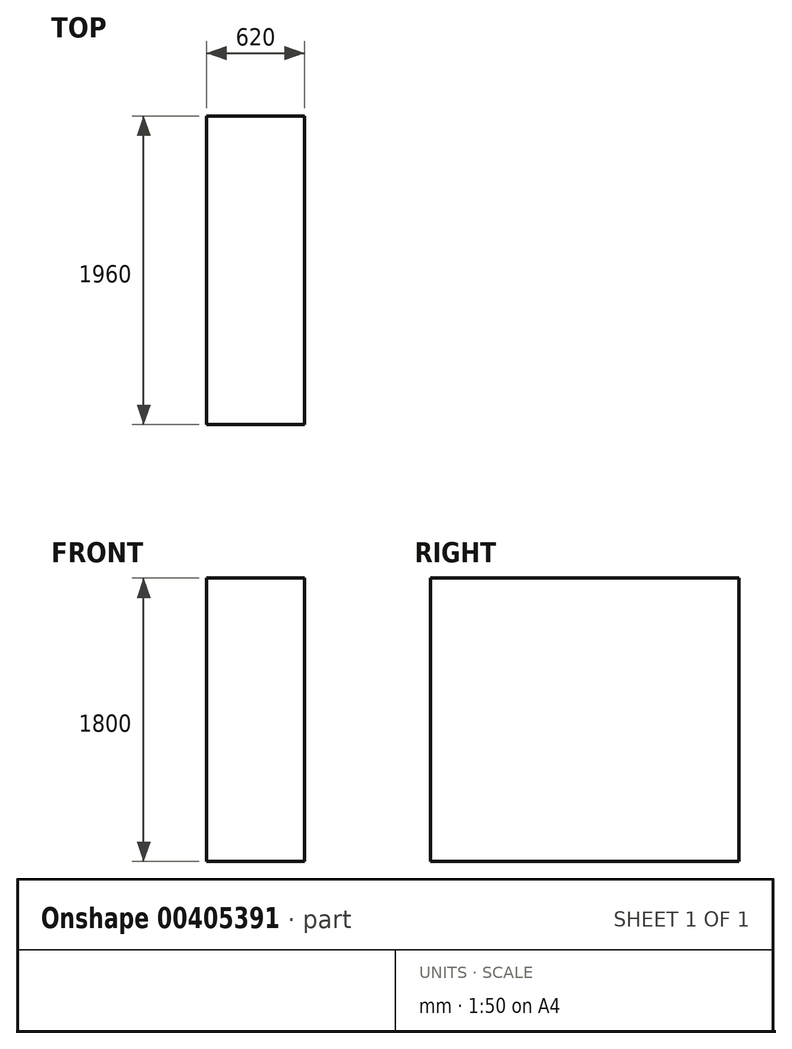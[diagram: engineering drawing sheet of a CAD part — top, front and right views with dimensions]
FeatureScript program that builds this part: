
annotation { "Feature Type Name" : "Feature", "Feature Type Description" : "" }
export const myFeature = defineFeature(function(context is Context, id is Id, definition is map)
    precondition{}
    {
        {
            var Q0;
            Q0=qCreatedBy(makeId("Top.planeOp"),FACE);
            var sketch = newSketch(context, id + "F0", { "sketchPlane" : qUnion([Q0])});
            skLineSegment(sketch, "E0.bottom", {"start": v(-570.83, 1900.38) * mm, "end": v(49.17, 1900.38) * mm});
            skLineSegment(sketch, "E0.top", {"start": v(-570.83, -59.62) * mm, "end": v(49.17, -59.62) * mm});
            skLineSegment(sketch, "E0.left", {"start": v(-570.83, 1900.38) * mm, "end": v(-570.83, -59.62) * mm});
            skLineSegment(sketch, "E0.right", {"start": v(49.17, 1900.38) * mm, "end": v(49.17, -59.62) * mm});
            skSolve(sketch);
        }
        {
            var Q0;
            Q0 = qSketchRegion(id + "F0", true);
            extrude(context, id + "F1", {"entities" : qUnion([Q0]), "depth" : 1800 * mm});
        }
    });
